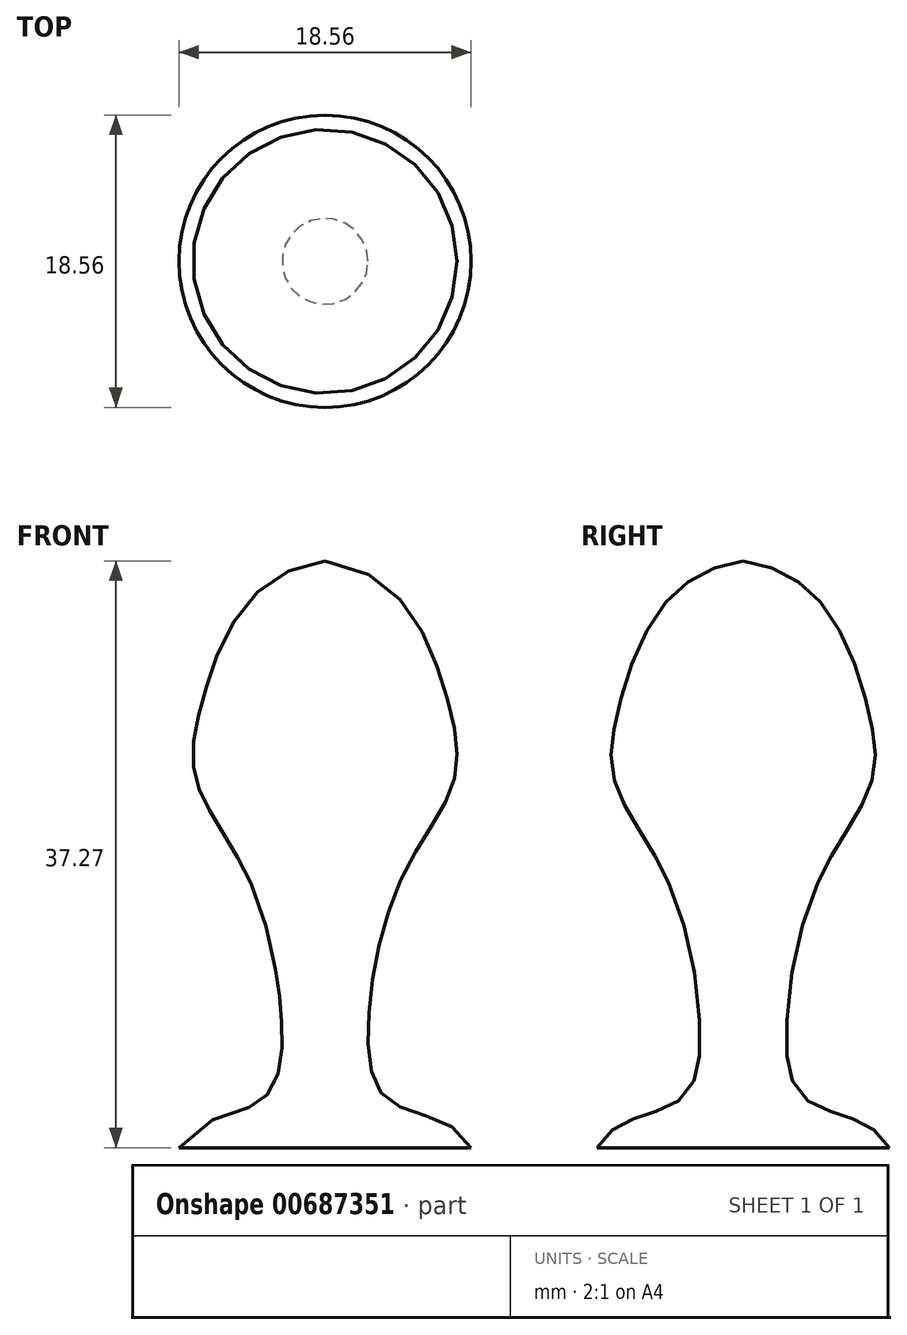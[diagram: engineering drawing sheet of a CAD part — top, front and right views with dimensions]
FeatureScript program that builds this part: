
annotation { "Feature Type Name" : "Feature", "Feature Type Description" : "" }
export const myFeature = defineFeature(function(context is Context, id is Id, definition is map)
    precondition{}
    {
        {
            var Q0;
            Q0=qCreatedBy(makeId("Front.planeOp"),FACE);
            var sketch = newSketch(context, id + "F0", { "sketchPlane" : qUnion([Q0])});
            skLineSegment(sketch, "E0", {"start": v(0, 0) * mm, "end": v(0, 37.27) * mm});
            skLineSegment(sketch, "E1", {"start": v(0, 0) * mm, "end": v(9.28, 0) * mm});
            skFitSpline(sketch, "E2", {"points": [v(9.28, 0) * mm, v(4.14, 2.94) * mm, v(2.76, 7.96) * mm, v(4.86, 17.11) * mm, v(8.12, 23.14) * mm, v(7.66, 28.88) * mm, v(0, 37.27) * mm], "startDerivative": vector(-19.87, 40.63) * mm, "endDerivative": vector(-73.15, 9.8) * mm});
            skSolve(sketch);
        }
        {
            var Q0;
            Q0=makeQuery(id+"F0.imprint","IMPRINT",FACE,{"disambiguationData":[TD([[makeQuery(id+"F0.imprint","IMPRINT",EDGE,{"derivedFrom":sQuery(id+"F0.wireOp",EDGE,"E0")}),-1.0]])]});
            var Q1;
            Q1=sQuery(id+"F0.wireOp",EDGE,"E0");
            revolve(context, id + "F1", {"entities" : qUnion([Q0]), "axis" : qUnion([Q1]), "revolveType" : RevolveType.FULL});
        }
    });
